# Revit family: FP_Revit_18_HC36_Downdraft_90001868A
name_source: partatom
category: Specialty Equipment
revit_build: Autodesk Revit 2018 (Build: 20170223_1515(x64)
units: mm (PartAtom-declared; Revit-internal decimal feet)

## family parameters
Always vertical = Yes
Cut with Voids When Loaded = Yes
OmniClass Number = 23.40.40.00
OmniClass Title = Food Service Equipment and Furnishings
Part Type = Normal
Room Calculation Point = No
Round Connector Dimension = Use Radius
Shared = No
Work Plane-Based = No

## types (4) — shared parameters
Cavity - Depth = 851 mm  [stored 2.79199 ft]
Cavity - Width = 343 mm  [stored 1.12533 ft]
Chassis - Depth = 838 mm
Chassis - Height = 730 mm  [stored 2.39501 ft]
Chassis - Width = 54 mm  [stored 0.177165 ft]
Connector Description - Electrical (Blower HBD600I) = 120 V, 60 Hz, 2.8 A
Connector Description - Electrical (Downdraft) = 120 V, 60 Hz, 15 Amp fused circuit
Manufacturer = Fisher & Paykel Appliances
Material - Body = Fisher & Paykel - Grey
Material - Trim = Fisher & Paykel - Stainless Steel
Product - Depth = 922 mm  [stored 3.02493 ft]
Product - Width = 108 mm  [stored 0.354331 ft]
URL = www.fisherpaykel.com
Visibility - Clearance Required = Yes

## per-type parameters (varying)
| type | Connector Description - Extraction | Model |
| HD36 with Blower HBD600I (Outlet Down) | 6” (152 mm) ducting, 600 CFM | HD36 Downdraft with Internal Blower HBD600I |
| HD36 with Blower HBD600I (Outlet Front) | 6” (152 mm) ducting, 600 CFM | HD36 Downdraft with Internal Blower HBD600I |
| HD36 without Blower | 10” (254 mm) ducting, 1200 CFM | HD36 Downdraft |
| HD36 with Blower HBD600I (Outlet Back) | 6” (152 mm) ducting, 600 CFM | HD36 Downdraft with Internal Blower HBD600I |

note: [stored X ft] marks values corroborated as IEEE doubles in the binary element streams (Revit-internal decimal feet)

## geometry (parser evidence)
native form markers: Sweep x2
no freeform markers — native parametric forms only
